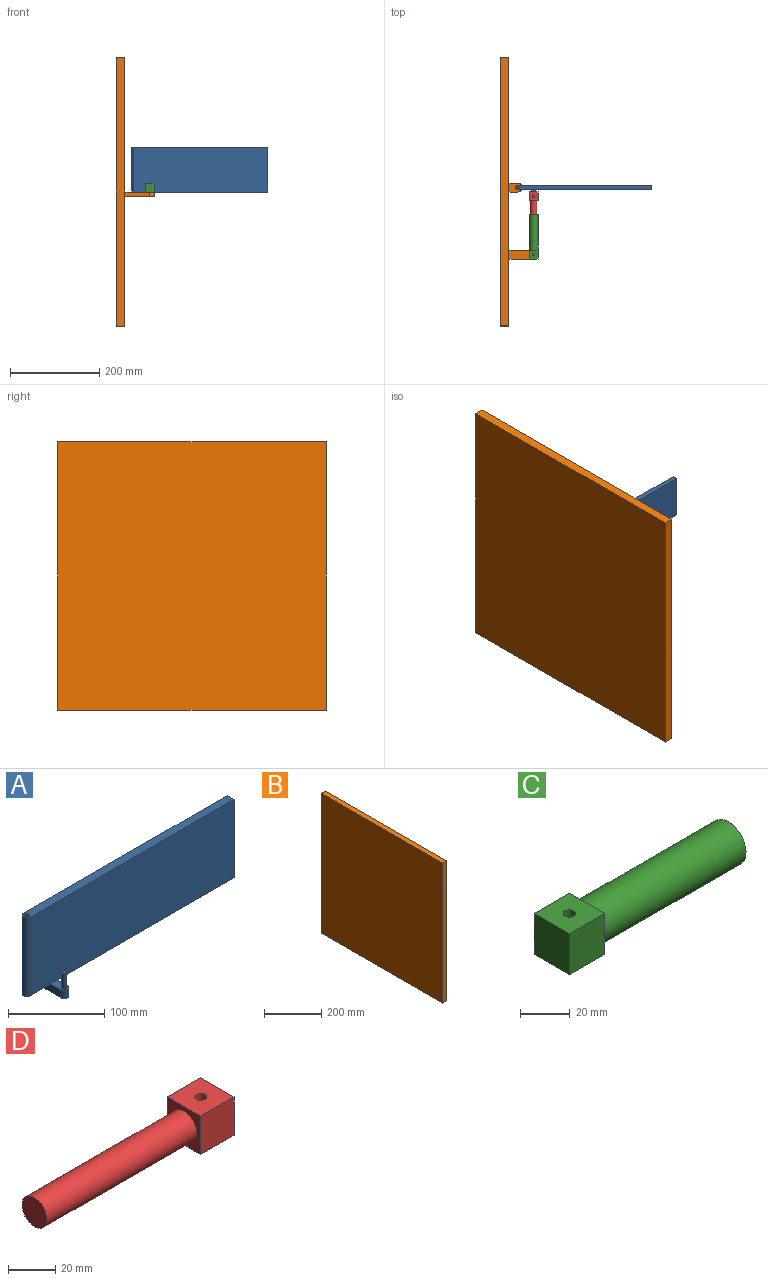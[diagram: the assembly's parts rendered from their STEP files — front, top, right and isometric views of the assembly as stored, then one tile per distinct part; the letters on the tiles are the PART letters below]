
ASSEMBLY  parts=4 mates=4
PART A: 15 faces, bbox 305x30x110 mm
  f0: plane 260x10mm, normal (0,0,-1), area 2600mm2, adj f1,f3,f5,f9
  f1: plane 300x110mm, normal (0,1,0), area 30100mm2, adj f0,f2,f5,f6,f7,f8,f9,f10
  f2: cylinder r=5mm len=100mm, axis (0,0,-1), area 1570.8mm2, adj f1,f3,f6,f7
  f3: plane 300x100mm, normal (0,-1,0), area 30000mm2, adj f0,f2,f5,f6,f7,f12
  f4: cylinder r=2.5mm len=100mm, axis (0,0,-1), area 1570.8mm2, adj f6,f7
  f5: plane 100x10mm, normal (1,0,0), area 1000mm2, adj f0,f1,f3,f6
  f6: plane 305x10mm, normal (0,0,1), area 3019.6mm2, adj f1,f2,f3,f4,f5
  f7: plane 35x10mm, normal (0,0,-1), area 319.6mm2, adj f1,f2,f3,f4,f8
  f8: plane 25x10mm, normal (-1,0,0), area 250mm2, adj f1,f7,f10,f11,f12
  f9: plane 25x10mm, normal (1,0,0), area 250mm2, adj f0,f1,f10,f11,f12
  f10: plane 30x10mm, normal (0,0,-1), area 289.3mm2, adj f1,f8,f9,f11
  f11: cylinder r=5mm len=10mm, axis (0,0,1), area 157.1mm2, adj f8,f9,f10,f12
  f12: plane 20x10mm, normal (0,0,1), area 169.6mm2, adj f3,f8,f9,f11,f13
  f13: cylinder r=2.5mm len=20mm, axis (0,0,-1), area 314.2mm2, adj f12,f14
  f14: plane 5x5mm, normal (0,0,1), area 19.6mm2, adj f13
PART B: 20 faces, bbox 85x600x600 mm
  f0: plane 600x600mm, normal (1,0,0), area 359600mm2, adj f1,f2,f3,f4,f6,f8,f9,f10
  f1: plane 600x20mm, normal (0,0,-1), area 12000mm2, adj f0,f2,f4,f5
  f2: plane 600x20mm, normal (0,1,0), area 12000mm2, adj f0,f1,f3,f5
  f3: plane 600x20mm, normal (0,0,1), area 12000mm2, adj f0,f2,f4,f5
  f4: plane 600x20mm, normal (0,-1,0), area 12000mm2, adj f0,f1,f3,f5
  f5: plane 600x600mm, normal (-1,0,0), area 360000mm2, adj f1,f2,f3,f4
  f6: plane 20x10mm, normal (0,-1,0), area 200mm2, adj f0,f7,f9,f10
  f7: cylinder r=10mm len=20mm, axis (0,0,1), area 314.2mm2, adj f6,f8,f9,f10
  f8: plane 20x10mm, normal (0,1,0), area 200mm2, adj f0,f7,f9,f10
  f9: plane 30x20mm, normal (0,0,-1), area 557.1mm2, adj f0,f6,f7,f8
  f10: plane 30x20mm, normal (0,0,1), area 537.4mm2, adj f0,f6,f7,f8,f16
  f11: plane 55x10mm, normal (0,-1,0), area 550mm2, adj f0,f12,f14,f15
  f12: cylinder r=10mm len=20mm, axis (0,0,1), area 314.2mm2, adj f11,f13,f14,f15
  f13: plane 55x10mm, normal (0,1,0), area 550mm2, adj f0,f12,f14,f15
  f14: plane 65x20mm, normal (0,0,-1), area 1257.1mm2, adj f0,f11,f12,f13
  f15: plane 65x20mm, normal (0,0,1), area 1237.4mm2, adj f0,f11,f12,f13,f18
  f16: cylinder r=2.5mm len=20mm, axis (0,0,-1), area 314.2mm2, adj f10,f17
  f17: plane 5x5mm, normal (0,0,1), area 19.6mm2, adj f16
  f18: cylinder r=2.5mm len=20mm, axis (0,0,-1), area 314.2mm2, adj f15,f19
  f19: plane 5x5mm, normal (0,0,1), area 19.6mm2, adj f18
PART C: 14 faces, bbox 100x20x20 mm
  f0: cylinder r=7.5mm len=80mm, axis (1,0,0), area 3769.9mm2, adj f2,f12
  f1: cylinder r=10mm len=80mm, axis (1,0,0), area 5026.5mm2, adj f2,f8,f9,f10,f11
  f2: plane 20x20mm, normal (1,0,0), area 137.4mm2, adj f0,f1
  f3: plane 20x20mm, normal (0,0,-1), area 380.4mm2, adj f4,f6,f7,f8,f11,f13
  f4: plane 20x20mm, normal (0,1,0), area 400mm2, adj f3,f5,f7,f10,f11
  f5: plane 20x20mm, normal (0,0,1), area 380.4mm2, adj f4,f6,f7,f9,f10,f13
  f6: plane 20x20mm, normal (0,-1,0), area 400mm2, adj f3,f5,f7,f8,f9
  f7: plane 20x20mm, normal (-1,0,0), area 400mm2, adj f3,f4,f5,f6
  f8: plane 10x10mm, normal (1,0,0), area 21.5mm2, adj f1,f3,f6
  f9: plane 10x10mm, normal (1,0,0), area 21.5mm2, adj f1,f5,f6
  f10: plane 10x10mm, normal (1,0,0), area 21.5mm2, adj f1,f4,f5
  f11: plane 10x10mm, normal (1,0,0), area 21.5mm2, adj f1,f3,f4
  f12: plane 15x15mm, normal (1,0,0), area 176.7mm2, adj f0
  f13: cylinder r=2.5mm len=20mm, axis (0,0,-1), area 314.2mm2, adj f3,f5
PART D: 9 faces, bbox 110x20x20 mm
  f0: cylinder r=7.5mm len=90mm, axis (-1,0,0), area 4241.2mm2, adj f1,f7
  f1: plane 15x15mm, normal (-1,0,0), area 176.7mm2, adj f0
  f2: plane 20x20mm, normal (0,0,-1), area 380.4mm2, adj f3,f5,f6,f7,f8
  f3: plane 20x20mm, normal (0,1,0), area 400mm2, adj f2,f4,f6,f7
  f4: plane 20x20mm, normal (0,0,1), area 380.4mm2, adj f3,f5,f6,f7,f8
  f5: plane 20x20mm, normal (0,-1,0), area 400mm2, adj f2,f4,f6,f7
  f6: plane 20x20mm, normal (1,0,0), area 400mm2, adj f2,f3,f4,f5
  f7: plane 20x20mm, normal (-1,0,0), area 223.3mm2, adj f0,f2,f3,f4,f5
  f8: cylinder r=2.5mm len=20mm, axis (0,0,-1), area 314.2mm2, adj f2,f4
PLACE A rot(axis=(0,0,1),0deg) t=(-245.19,-34.9,138.83)mm
PLACE B t=(-265.19,-44.9,138.83)mm fixed
PLACE C rot(axis=(0,0,1),90deg) t=(-210.19,-94.9,148.83)mm
PLACE D rot(axis=(0,0,1),90deg) t=(-210.19,-174.9,148.83)mm
MATE revolute D.f8 <-> A.f11  axis (0,0,-1) through (-210.19,-54.9,138.83)mm
MATE revolute A.f2 <-> B.f7  axis (0,0,-1) through (-245.19,-34.9,138.83)mm
MATE revolute C.f13 <-> B.f12  axis (0,0,-1) through (-210.19,-184.9,138.83)mm
MATE slider C.f1 <-> D.f0  axis (0,-1,0) through (-210.19,-174.9,148.83)mm
